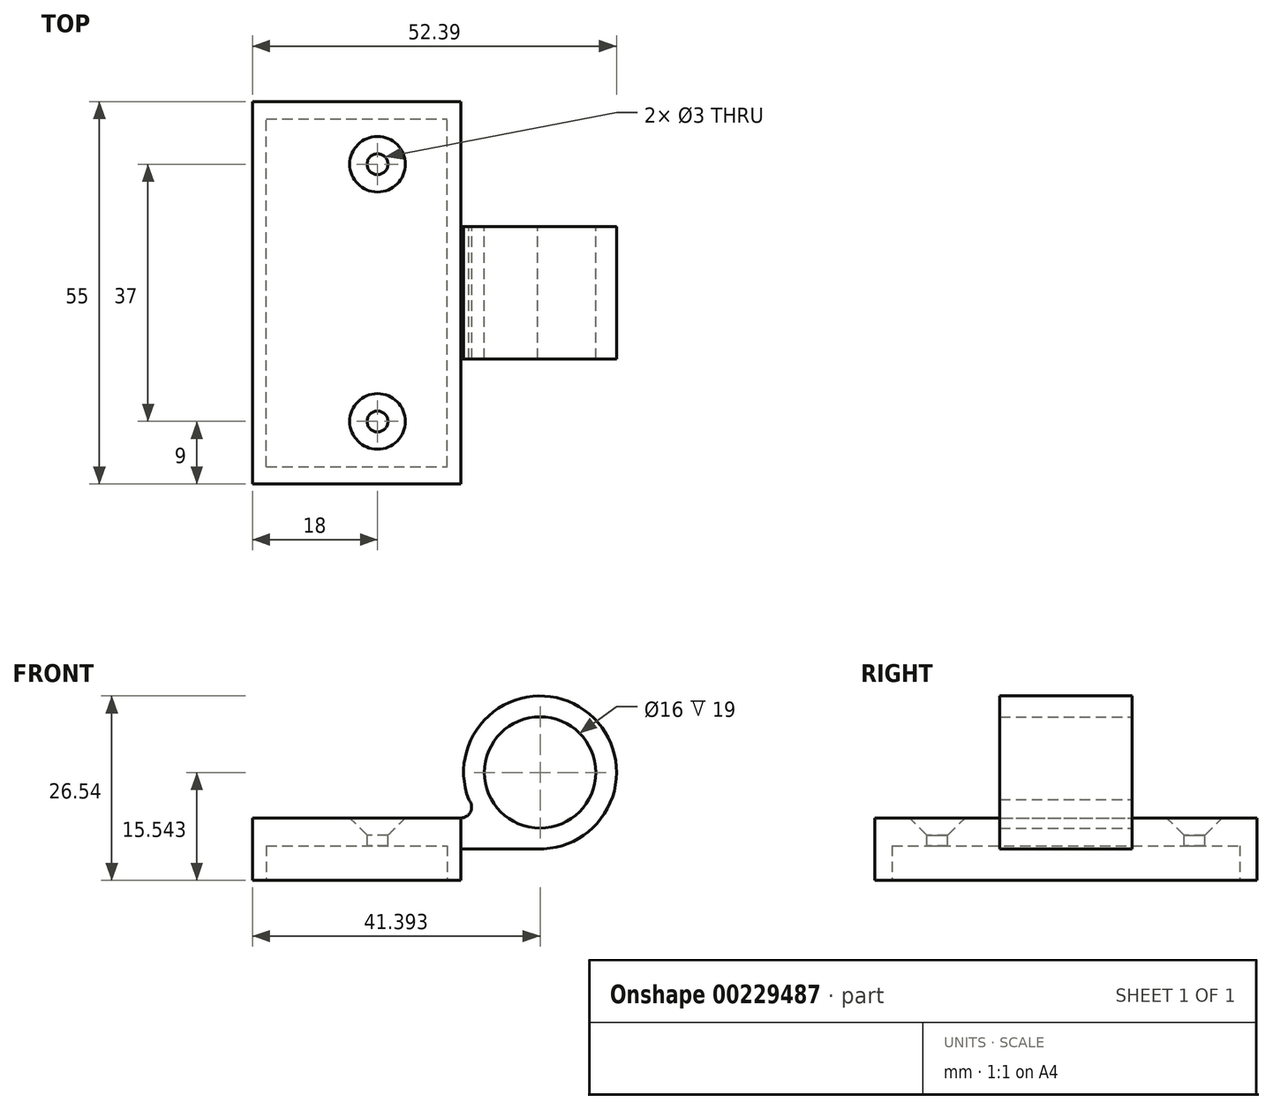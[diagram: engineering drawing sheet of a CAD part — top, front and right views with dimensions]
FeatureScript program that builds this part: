
annotation { "Feature Type Name" : "Feature", "Feature Type Description" : "" }
export const myFeature = defineFeature(function(context is Context, id is Id, definition is map)
    precondition{}
    {
        {
            var Q0;
            Q0=qCreatedBy(makeId("Front.planeOp"),FACE);
            var sketch = newSketch(context, id + "F0", { "sketchPlane" : qUnion([Q0])});
            skLineSegment(sketch, "E0.bottom", {"start": v(-15, -4.5) * mm, "end": v(15, -4.5) * mm});
            skLineSegment(sketch, "E0.top", {"start": v(-15, 4.5) * mm, "end": v(15, 4.5) * mm});
            skLineSegment(sketch, "E0.left", {"start": v(-15, -4.5) * mm, "end": v(-15, 4.5) * mm});
            skLineSegment(sketch, "E0.right", {"start": v(15, -4.5) * mm, "end": v(15, 4.5) * mm});
            skPoint(sketch, "E0.middle", {"position": v(0, 0) * mm});
            skCircle(sketch, "E1", {"center": v(26.4, 11.04) * mm, "radius": 11 * mm});
            skLineSegment(sketch, "E2", {"start": v(26.03, 0.05) * mm, "end": v(15, 0.05) * mm});
            skArc(sketch, "E3", {"start": v(15, 4.5) * mm, "mid": v(16.43, 5.45) * mm, "end": v(16.11, 7.13) * mm});
            skCircle(sketch, "E4", {"center": v(26.4, 11.04) * mm, "radius": 8 * mm});
            skSolve(sketch);
        }
        {
            var Q0;
            {var subQ1=sQuery(id+"F0.wireOp",EDGE,"E0.bottom");Q0=makeQuery(id+"F0.imprint","IMPRINT",FACE,{"disambiguationData":[TD([[makeQuery(id+"F0.imprint","IMPRINT",EDGE,{"derivedFrom":subQ1}),1.0]])]});}
            extrude(context, id + "F1", {"entities" : qUnion([Q0]), "endBound" : BoundingType.SYMMETRIC, "depth" : 55 * mm});
        }
        {
            var Q0;
            {var subQ3=sQuery(id+"F0.wireOp",EDGE,"E2");Q0=makeQuery(id+"F0.imprint","IMPRINT",FACE,{"disambiguationData":[TD([[makeQuery(id+"F0.imprint","IMPRINT",EDGE,{"derivedFrom":subQ3}),-1.0]])]});}
            var Q1;
            Q1=makeQuery(id+"F0.imprint","IMPRINT",FACE,{"disambiguationData":[TD([[makeQuery(id+"F0.imprint","IMPRINT",EDGE,{"derivedFrom":sQuery(id+"F0.wireOp",EDGE,"E4")}),-1.0]])]});
            extrude(context, id + "F2", {"entities" : qUnion([Q0, Q1]), "endBound" : BoundingType.SYMMETRIC, "depth" : 19 * mm});
        }
        {
            var Q0;
            Q0=makeQuery(id+"F1.opExtrude","SWEPT_FACE",FACE,{"disambiguationData":[OSD([sQuery(id+"F0.wireOp",EDGE,"E0.top")])]});
            var sketch = newSketch(context, id + "F3", { "sketchPlane" : qUnion([Q0])});
            skSolve(sketch);
        }
        {
            var Q0;
            {var subQ0=sQuery(id+"F0.wireOp",EDGE,"E0.top");Q0=makeQuery(id+"F3.imprint","IMPRINT",FACE,{"disambiguationData":[TD([[makeQuery(id+"F3.imprint","IMPRINT",EDGE,{"derivedFrom":makeQuery(id+"F1.opExtrude","CAP_EDGE",EDGE,{"disambiguationData":[OSD([subQ0])],"isStart":true})}),-1.0]])]});}
            var sketch = newSketch(context, id + "F4", { "sketchPlane" : qUnion([Q0])});
            skLineSegment(sketch, "E5.0", {"start": v(-15, 18.5) * mm, "end": v(15, 18.5) * mm});
            skLineSegment(sketch, "E6.0", {"start": v(-15, -18.5) * mm, "end": v(15, -18.5) * mm});
            skLineSegment(sketch, "E7.0", {"start": v(3, -27.5) * mm, "end": v(3, 27.5) * mm});
            skCircle(sketch, "E8", {"center": v(3, 18.5) * mm, "radius": 1.5 * mm});
            skPoint(sketch, "E8.centerSnap0", {"position": v(0, 18.5) * mm});
            skCircle(sketch, "E9", {"center": v(3, -18.5) * mm, "radius": 1.5 * mm});
            skSolve(sketch);
        }
        {
            var Q0;
            Q0=sQuery(id+"F4.wireOp",VERTEX,"E8.center");
            var Q1;
            Q1=sQuery(id+"F4.wireOp",VERTEX,"E9.center");
            var Q2;
            Q2=makeQuery(id+"F1.opExtrude","SWEPT_BODY",BODY,{"disambiguationData":[OSD([sQuery(id+"F0.wireOp",EDGE,"E0.bottom"),sQuery(id+"F0.wireOp",EDGE,"E0.top"),sQuery(id+"F0.wireOp",EDGE,"E0.left"),sQuery(id+"F0.wireOp",EDGE,"E0.right")])]});
            hole(context, id + "F5", {"style" : HoleStyle.C_SINK, "endStyle" : HoleEndStyle.THROUGH, "holeDiameter" : 3 * mm, "cSinkDiameter" : 8 * mm, "cSinkAngle" : 90 * degree, "startFromSketch" : true, "locations" : qUnion([Q0, Q1]), "scope" : qUnion([Q2]), "isTappedThrough" : true});
        }
        {
            var Q0;
            Q0=makeQuery(id+"F1.opExtrude","SWEPT_FACE",FACE,{"disambiguationData":[OSD([sQuery(id+"F0.wireOp",EDGE,"E0.bottom")])]});
            var sketch = newSketch(context, id + "F6", { "sketchPlane" : qUnion([Q0])});
            skLineSegment(sketch, "E10.bottom", {"start": v(-13, 25) * mm, "end": v(13, 25) * mm});
            skLineSegment(sketch, "E10.top", {"start": v(-13, -25) * mm, "end": v(13, -25) * mm});
            skLineSegment(sketch, "E10.left", {"start": v(-13, 25) * mm, "end": v(-13, -25) * mm});
            skLineSegment(sketch, "E10.right", {"start": v(13, 25) * mm, "end": v(13, -25) * mm});
            skPoint(sketch, "E10.middle", {"position": v(0, 0) * mm});
            skSolve(sketch);
        }
        {
            var Q0;
            Q0=makeQuery(id+"F6.imprint","IMPRINT",FACE,{"disambiguationData":[TD([[makeQuery(id+"F6.imprint","IMPRINT",EDGE,{"derivedFrom":sQuery(id+"F6.wireOp",EDGE,"E10.bottom")}),-1.0]])]});
            extrude(context, id + "F7", {"entities" : qUnion([Q0]), "operationType" : NewBodyOperationType.REMOVE, "oppositeDirection" : true, "depth" : 5 * mm});
        }
    });
